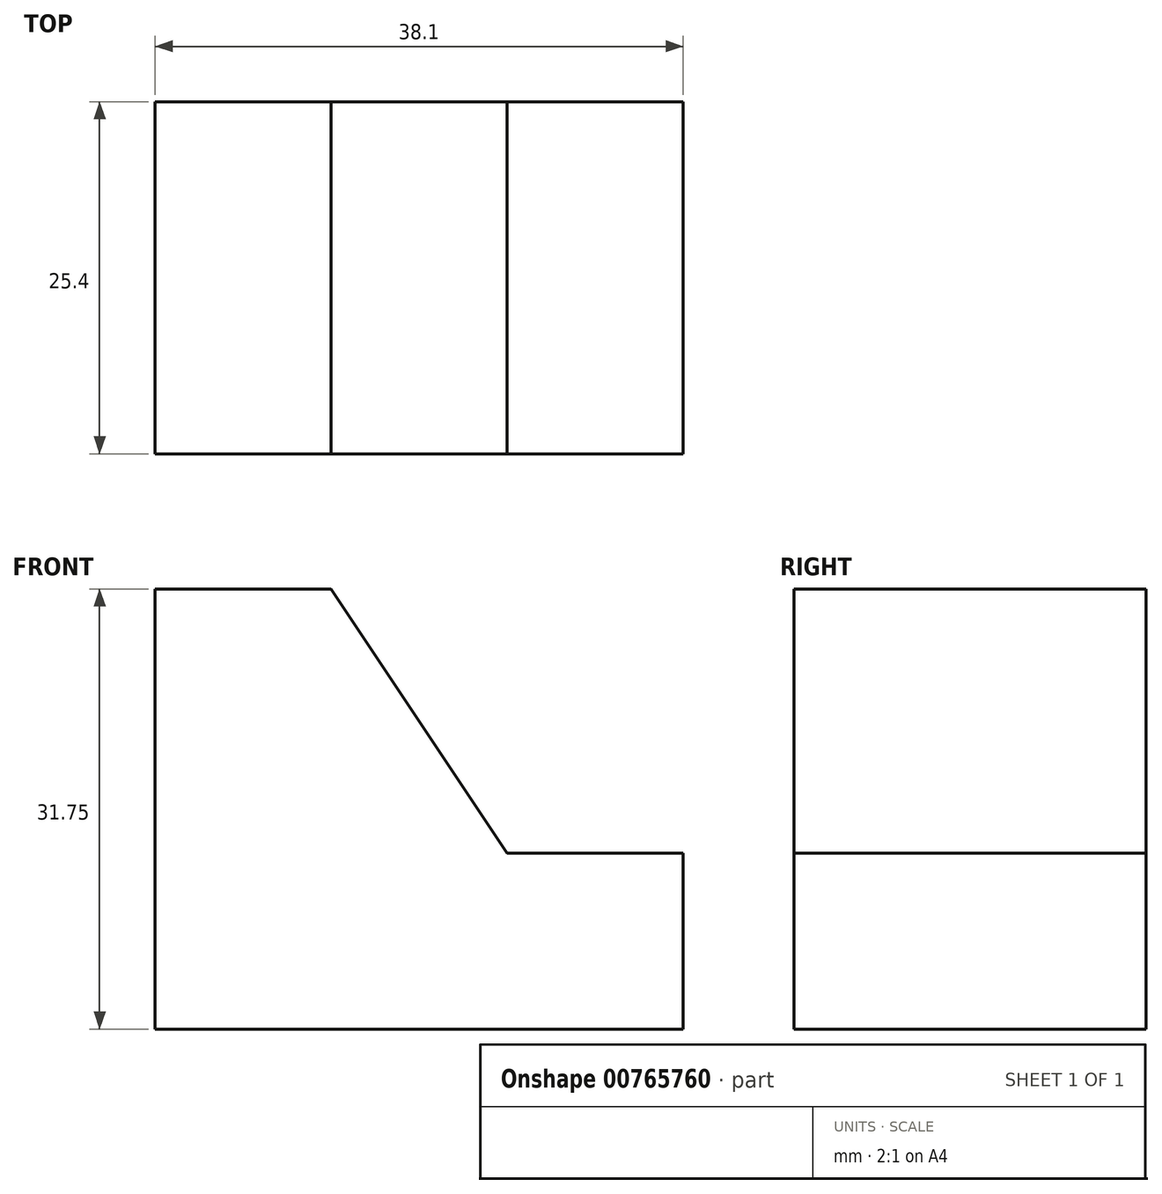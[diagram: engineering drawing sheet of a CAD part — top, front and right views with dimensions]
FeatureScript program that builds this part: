
annotation { "Feature Type Name" : "Feature", "Feature Type Description" : "" }
export const myFeature = defineFeature(function(context is Context, id is Id, definition is map)
    precondition{}
    {
        {
            var Q0;
            Q0=qCreatedBy(makeId("Front.planeOp"),FACE);
            var sketch = newSketch(context, id + "F0", { "sketchPlane" : qUnion([Q0])});
            skLineSegment(sketch, "E0", {"start": v(0, 0) * mm, "end": v(-12.7, 0) * mm});
            skLineSegment(sketch, "E1", {"start": v(-12.7, 0) * mm, "end": v(-12.7, -31.75) * mm});
            skLineSegment(sketch, "E2", {"start": v(-12.7, -31.75) * mm, "end": v(25.4, -31.75) * mm});
            skLineSegment(sketch, "E3", {"start": v(25.4, -31.75) * mm, "end": v(25.4, -19.05) * mm});
            skLineSegment(sketch, "E4", {"start": v(25.4, -19.05) * mm, "end": v(12.7, -19.05) * mm});
            skLineSegment(sketch, "E5", {"start": v(12.7, -19.05) * mm, "end": v(0, 0) * mm});
            skSolve(sketch);
        }
        {
            var Q0;
            Q0 = qSketchRegion(id + "F0", true);
            extrude(context, id + "F1", {"entities" : qUnion([Q0]), "depth" : 25.4 * mm, "offsetDistance" : 25.4 * mm});
        }
    });
